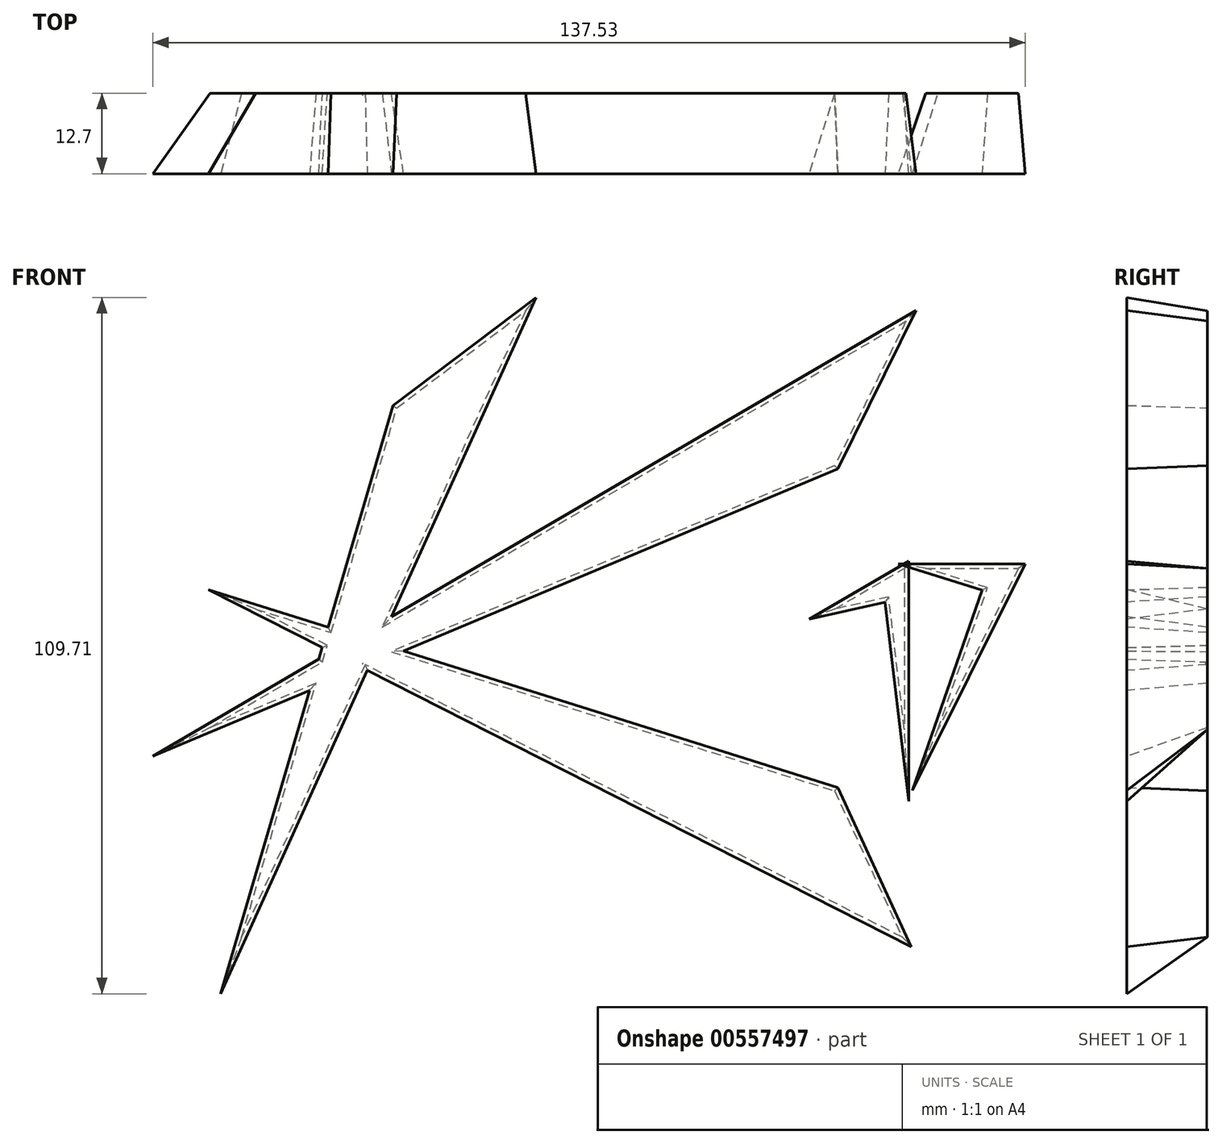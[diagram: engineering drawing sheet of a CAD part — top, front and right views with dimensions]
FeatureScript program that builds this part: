
annotation { "Feature Type Name" : "Feature", "Feature Type Description" : "" }
export const myFeature = defineFeature(function(context is Context, id is Id, definition is map)
    precondition{}
    {
        {
            var Q0;
            Q0=qCreatedBy(makeId("Front.planeOp"),FACE);
            var sketch = newSketch(context, id + "F0", { "sketchPlane" : qUnion([Q0])});
            skLineSegment(sketch, "E0", {"start": v(-43.47, -11.01) * mm, "end": v(-43.52, -11.09) * mm});
            skLineSegment(sketch, "E1", {"start": v(-67.5, -21.14) * mm, "end": v(42.16, 42.9) * mm});
            skLineSegment(sketch, "E2", {"start": v(-67.5, -21.14) * mm, "end": v(30.93, 20.12) * mm});
            skLineSegment(sketch, "E3", {"start": v(42.16, 42.9) * mm, "end": v(30.93, 20.12) * mm});
            skLineSegment(sketch, "E4", {"start": v(41.6, -54.2) * mm, "end": v(-60.33, -2.46) * mm});
            skLineSegment(sketch, "E5", {"start": v(41.6, -54.2) * mm, "end": v(30.93, -31.14) * mm});
            skLineSegment(sketch, "E6", {"start": v(30.93, -31.14) * mm, "end": v(-60.33, -2.46) * mm});
            skLineSegment(sketch, "E7", {"start": v(30.93, -2.46) * mm, "end": v(41.9, 3.95) * mm});
            skLineSegment(sketch, "E8", {"start": v(41.9, 3.95) * mm, "end": v(41.9, -21.45) * mm});
            skLineSegment(sketch, "E9", {"start": v(41.9, -21.45) * mm, "end": v(39.1, 2.31) * mm});
            skLineSegment(sketch, "E10", {"start": v(30.93, -2.46) * mm, "end": v(41.9, 0) * mm});
            skLineSegment(sketch, "E11", {"start": v(59.9, 3.95) * mm, "end": v(47.2, -21.45) * mm});
            skLineSegment(sketch, "E12", {"start": v(45.28, 3.95) * mm, "end": v(57.92, 0) * mm});
            skLineSegment(sketch, "E13", {"start": v(47.2, -21.45) * mm, "end": v(56.05, 3.95) * mm});
            skPoint(sketch, "E14.orphan", {"position": v(47.2, 3.95) * mm});
            skLineSegment(sketch, "E15", {"start": v(-62.55, -54.2) * mm, "end": v(-17.8, 44.52) * mm});
            skLineSegment(sketch, "E16", {"start": v(-62.55, -54.2) * mm, "end": v(-38.09, 29.23) * mm});
            skLineSegment(sketch, "E17", {"start": v(-38.09, 29.23) * mm, "end": v(-17.8, 44.52) * mm});
            skLineSegment(sketch, "E18", {"start": v(45.28, 3.95) * mm, "end": v(59.9, 3.95) * mm});
            skSolve(sketch);
        }
        {
            var Q0;
            Q0 = qSketchRegion(id + "F0", true);
            var Q1;
            {var subQ0=sQuery(id+"F0.wireOp",EDGE,"E4");var subQ2=sQuery(id+"F0.wireOp",EDGE,"E1");var subQ3=makeQuery(id+"F0.imprint","INTERSECT",VERTEX,{"derivedFrom":[subQ2,subQ0]});Q1=makeQuery(id+"F0.imprint","IMPRINT",FACE,{"disambiguationData":[TD([[makeQuery(id+"F0.imprint","IMPRINT",EDGE,{"disambiguationData":[TD([[subQ3,-1.0]])],"derivedFrom":subQ2}),-1.0]])]});}
            extrude(context, id + "F1", {"entities" : qUnion([Q0, Q1]), "depth" : 12.7 * mm, "offsetDistance" : 25.4 * mm, "hasDraft" : true, "draftAngle" : 3 * degree});
        }
    });
